# Revit family: NBS_DuPontCorian_IntegrtdWshBsns_BathSink_Peace-7610
name_source: partatom
category: Plumbing Fixtures
revit_build: Autodesk Revit 2014 (Build: 20130709_2115(x64)
units: mm (PartAtom-declared; Revit-internal decimal feet)

## types (1)
- 7610
    AccessibilityPerformance = http://www.dupont.co.uk
    AssetType = Fixed
    BIMObjectName = NBS_DuPontCorian_IntegtdWashBasins_BathSink_Peace7610
    BasinLength = 590 mm  [stored 1.9357 ft]
    BasinWidth = 368 mm  [stored 1.20735 ft]
    BottomCornerRadius = 70
    Category = Pr_40_20_96_18 : Integrated wash basins
    Color = Designer White, Glacier White
    CounterThickness = 40 mm  [stored 0.131234 ft]
    CounterVoidLength = 565 mm  [stored 1.85367 ft]
    CounterVoidWidth = 343 mm  [stored 1.12533 ft]
    DeclarationOfPerformance = CL 25 - EN 14688:2006
    Default Elevation = 1219 mm
    Description = Solid surface Corian(R) rectangular symmetrical basin with curved corners. Corian(R) is a flexible composite material manufactured from natural minerals and acrylic resin. Designed to be seamlessly integrated into a Corian(R) surface.
    DrainSize = 47 mm
    DurationUnit = 40 years plus
    ExpectedLife = 40 years plus
    Features = Designed to be integrated into a Corian(R) worksurface. Available in the full colour range as standard or bespoke colours. Hygienic,  easy to clean and maintain. Inconspicuous joints.
    Finish = Semi-gloss
    Form = Inset & Integrated into surface or mounted under surface (undermount)
    IfcExportAs = IfcSanitaryTerminalType
    IfcExportType = WASHHANDBASIN
    IntegralAccessories = Includes overflow piece & 25mm diameter overflow elbow
    InternalDepth = 130
    InternalLength = 540
    InternalWidth = 320
    ManufacturerName = DuPont Corian
    ManufacturerURL = www.dupont.co.uk
    Material = DuPont™ Corian® solid surface material (natural minerals & acrylic resin composite)
    ModelNumber = Peace 7610
    ModelReference = Peace 7610
    NBSCertification = http://www.nationalbimlibrary.com
    NBSDescription = Sinks
    NBSReference = 45-35-70/360
    Name = IntegratedWashBasins_-7610_DuPontCorian
    NominalDepth = 167 mm
    NominalHeight = 0 mm  [stored 0 ft]
    NominalLength = 368 mm  [stored 1.20735 ft]
    NominalWidth = 590 mm  [stored 1.9357 ft]
    OutletMaterial = NBS_Concept
    ProductInformation = www.dupont.co.uk/content/dam/dupont/products-and-services/construction-materials/surface-design-materials/documents/DuPont_Corian_Kitchen_and_Bathroom_Product_catalogue.pdf
    ReplacementCost = Repairable
    Shape = Rectangular
    SinkMaterial = NBS_Concept
    SinkMounting = Integrated into worksurface or mounted under worksurface (undermount)
    SinkType = Hand Rinse. Tailormade & bespoke options available. Suitable for dental/hospital environments.
    Size = 590 x 368 x 167 mm
    SustainabilityPerformance = ISO 14001. Zero landfill at manufacturing site. Greenguard certified. Repairable nature makes lifetime performance 40 years plus.
    TopCornerRadius = 78
    Uniclass2 = 45-31-79/418
    Uniclass2015Description = Wash basins
    Uniclass2015Reference = Pr_40_20_96_18
    Uniclass2015Version = Products v1.1
    Version = 1
    WarrantyDescription = 10 year material warranty from DuPont(TM)
    WarrantyDurationParts = 10 years
    WarrantyDurationUnit = year
    WasteOutletDiameter = 47 mm
    WaterSupplyOverflowAndWasteHolesOverflow = Round overflow hole with cover
    WaterSupplyOverflowAndWasteHolesWaste = No tapholes
    WaterSupplyOverflowAndWasteHolesWaterSupply = Round bottom waste outlet with drain cover

note: [stored X ft] marks values corroborated as IEEE doubles in the binary element streams (Revit-internal decimal feet)

## geometry (parser evidence)
native form markers: Sweep x3
no freeform markers — native parametric forms only
